# Revit family: Door-Hardware_Hinge_Hager_Stainless-Continuous
name_source: partatom
category: Specialty Equipment
units: mm (PartAtom-declared; Revit-internal decimal feet)

## family parameters
Always vertical = No
Cut with Voids When Loaded = No
Enable Cutting in Views = No
Maintain Annotation Orientation = No
OmniClass Number = 23.30.40.24.11
OmniClass Title = Hinges
Part Type = Normal
Room Calculation Point = No
Round Connector Dimension = Use Diameter
Shared = Yes
Work Plane-Based = Yes

## types (9) — shared parameters
Assembly Code = C1020410
Available Options = as Specified
Capacity = as Specified
Clearance Required = 0' - 0"
Default Elevation = 0' - 0"
Hinge Design = Hinge
Keynote = 087100
Manufacturer = Hager Companies
Manufacturer Fax = 800-782-0149
Manufacturer Website = http://www.hagerco.com
Product Data = http://www.arcat.com
Restrictions = as Specified
Revision = R1_2015-10
Sales Information = http://www.hagerco.com
Specification = http://www.arcat.com
Standards Conformance = as Specified
Suggested Use = as Specified
URL = http://www.hagerco.com
zero-valued in all types: Expected Lifespan (Years), Maintenance Schedule (Months), Warranty Duration (Years)

## per-type parameters (varying)
| type | Description | Hinge Depth | Hinge Width | Model |
| Full Surface 909 | Hager Standard Duty Stainless Steel Continuous Hinge - Full Surface 790-909 as Specified | 0' - 0 3/4" | 0' - 3 1/2" | 790-909 |
| Half Mortise 906 | Hager Standard Duty Stainless Steel Continuous Hinge - Half Mortise 790-906 as Specified | 0' - 0 3/4" | 0' - 1 7/8" | 790-906 |
| Half Mortise 904 | Hager Standard Duty Stainless Steel Continuous Hinge - Half Mortise 790-904 as Specified | 0' - 0 3/4" | 0' - 1 7/8" | 790-904 |
| Half Surface 903 | Hager Standard Duty Stainless Steel Continuous Hinge - Half Surface 790-903 as Specified | 0' - 0 1/2" | 0' - 1 7/8" | 790-903 |
| Concealed Swing Clear 911 | Hager Standard Duty Stainless Steel Continuous Hinge - Concealed Swing Clear 790-911 as Specified | 0' - 0 7/16" | 0' - 2" | 790-911 |
| Concealed Swing Clear Corner Guard 926 | Hager Standard Duty Stainless Steel Continuous Hinge - Concealed Swing Clear 790-926 as Specified | 0' - 0 7/16" | 0' - 2" | 790-926 |
| Concealed Corner Wrap 915 | Hager Standard Duty Stainless Steel Continuous Hinge - Concealed 790-915 as Specified | 0' - 0 1/2" | 0' - 0 3/8" | 790-915 |
| Concealed Corner Guard 905 | Hager Standard Duty Stainless Steel Continuous Hinge - Concealed 790-905 as Specified | 0' - 0 1/2" | 0' - 0 3/8" | 790-905 |
| Concealed 900 | Hager Standard Duty Stainless Steel Continuous Hinge - Concealed 790-900 as Specified | 0' - 0 1/2" | 0' - 0 3/8" | 790-900 |

## geometry (parser evidence)
native form markers: Blend x6, Sweep x4
no freeform markers — native parametric forms only
